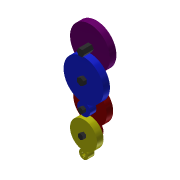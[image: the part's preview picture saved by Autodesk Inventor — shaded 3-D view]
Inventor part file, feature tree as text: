
AUTODESK INVENTOR PART (.ipt)
format: ipt  version: 2015 (Build 190159000, 159)  size: 228,352 bytes
history: native  units: in
note: dims shown in document units (in); Inventor stores cm internally (conversion verified against a paired STEP export)
features: other x5, extrude x5, sketch x1
ambient origin geometry x8: Origin, YZ Plane, XZ Plane, XY Plane, X Axis, Y Axis, Z Axis, Center Point
bodies: Body1 (feature_tree), Body2 (feature_tree), Body3 (feature_tree), Body4 (feature_tree), Body5 (feature_tree)
feature tree (11):
  other  "Stage1"
  sketch  "Sketch1"  dims[d0=0.6in d1=2.5in d2=0.7in d3=2.0in d4=1.303in d5=1.0in d6=2.5in d7=1.753in d8=0.9in d9=3.0in d10=1.953in d11=0.9in d12=3.0in d13=1.953in d14=1.1in d15=2.1in d18=1.0in d19=2.6in d20=1.0in d21=3.1in d22=3.1in d23=0.375in d24=0.5in d25=0.313in d26=0.0787in d27=0.5in d28=0.0in d31=0.5in d32=0.0in d33=0.5in d34=0.0in d35=0.5in d36=0.0in d37=1.5in d38=0.0in d39=0.5in]
  extrude  "Extrusion2"  Depth=0.5in
  extrude  "Extrusion4"  Depth=0.5in
  extrude  "Extrusion5"  Depth=0.5in
  extrude  "Extrusion6"  Depth=1.303in
  extrude  "Extrusion7"  Depth=1.0in
  other  "Stage2"
  other  "Stage3"
  other  "Stage4"
  other  "axles"
